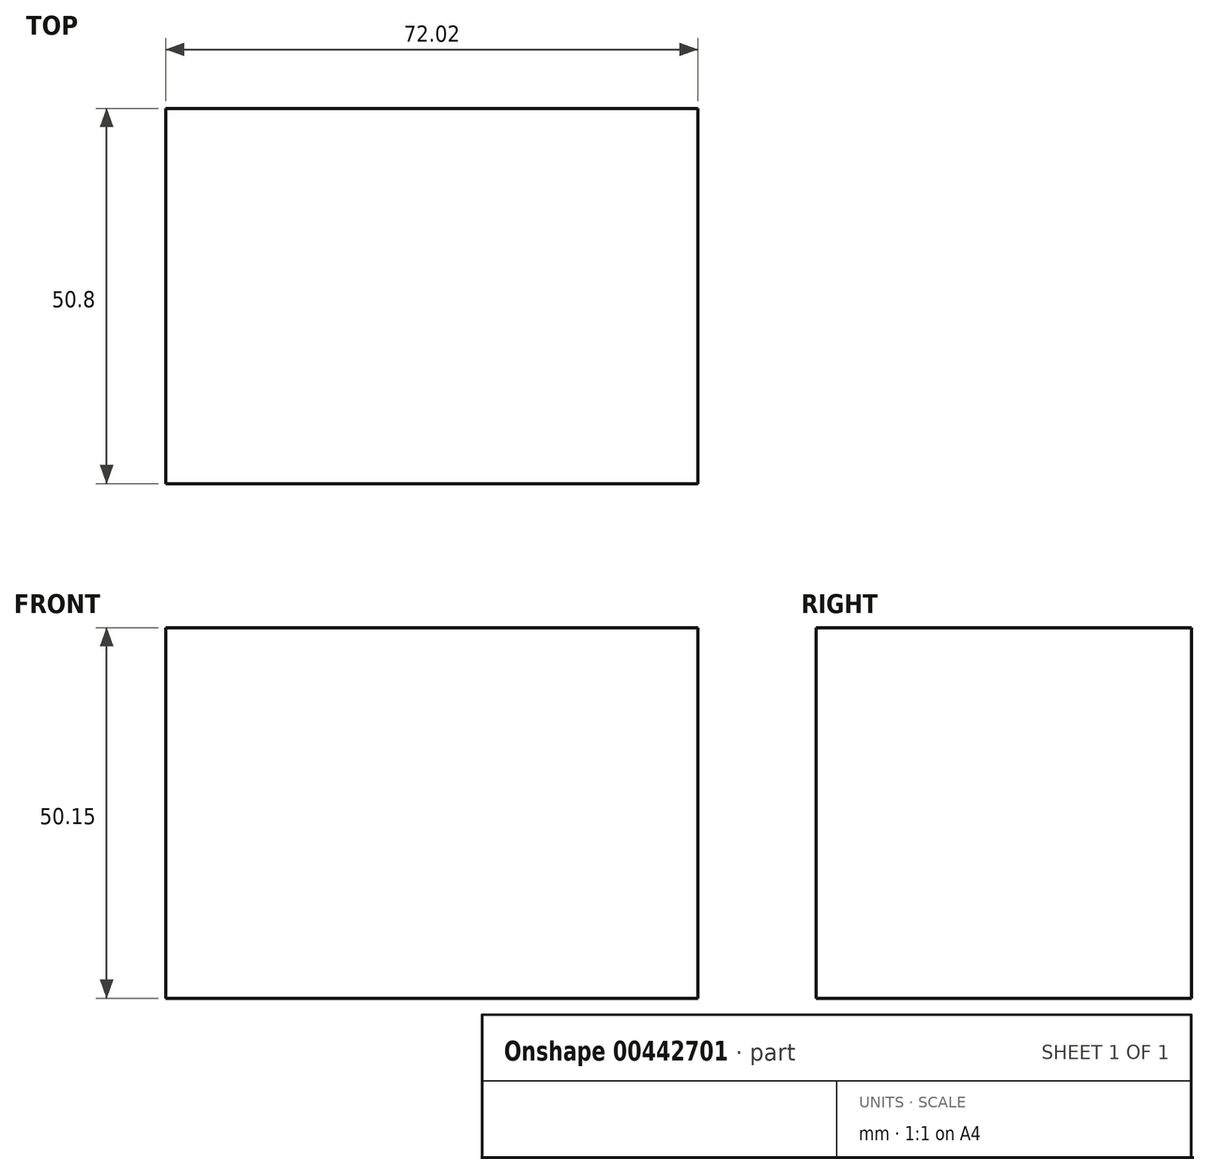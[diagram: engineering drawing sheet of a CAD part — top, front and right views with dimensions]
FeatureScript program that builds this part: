
annotation { "Feature Type Name" : "Feature", "Feature Type Description" : "" }
export const myFeature = defineFeature(function(context is Context, id is Id, definition is map)
    precondition{}
    {
        {
            var Q0;
            Q0=qCreatedBy(makeId("Front.planeOp"),FACE);
            var sketch = newSketch(context, id + "F0", { "sketchPlane" : qUnion([Q0])});
            skLineSegment(sketch, "E0.bottom", {"start": v(-42.32, 34.5) * mm, "end": v(29.7, 34.5) * mm});
            skLineSegment(sketch, "E0.top", {"start": v(-42.32, -15.65) * mm, "end": v(29.7, -15.65) * mm});
            skLineSegment(sketch, "E0.left", {"start": v(-42.32, 34.5) * mm, "end": v(-42.32, -15.65) * mm});
            skLineSegment(sketch, "E0.right", {"start": v(29.7, 34.5) * mm, "end": v(29.7, -15.65) * mm});
            skSolve(sketch);
        }
        {
            var Q0;
            Q0=makeQuery(id+"F0.imprint","IMPRINT",FACE,{"disambiguationData":[TD([[makeQuery(id+"F0.imprint","IMPRINT",EDGE,{"derivedFrom":sQuery(id+"F0.wireOp",EDGE,"E0.bottom")}),-1.0]])]});
            extrude(context, id + "F1", {"entities" : qUnion([Q0]), "depth" : 50.8 * mm});
        }
    });
